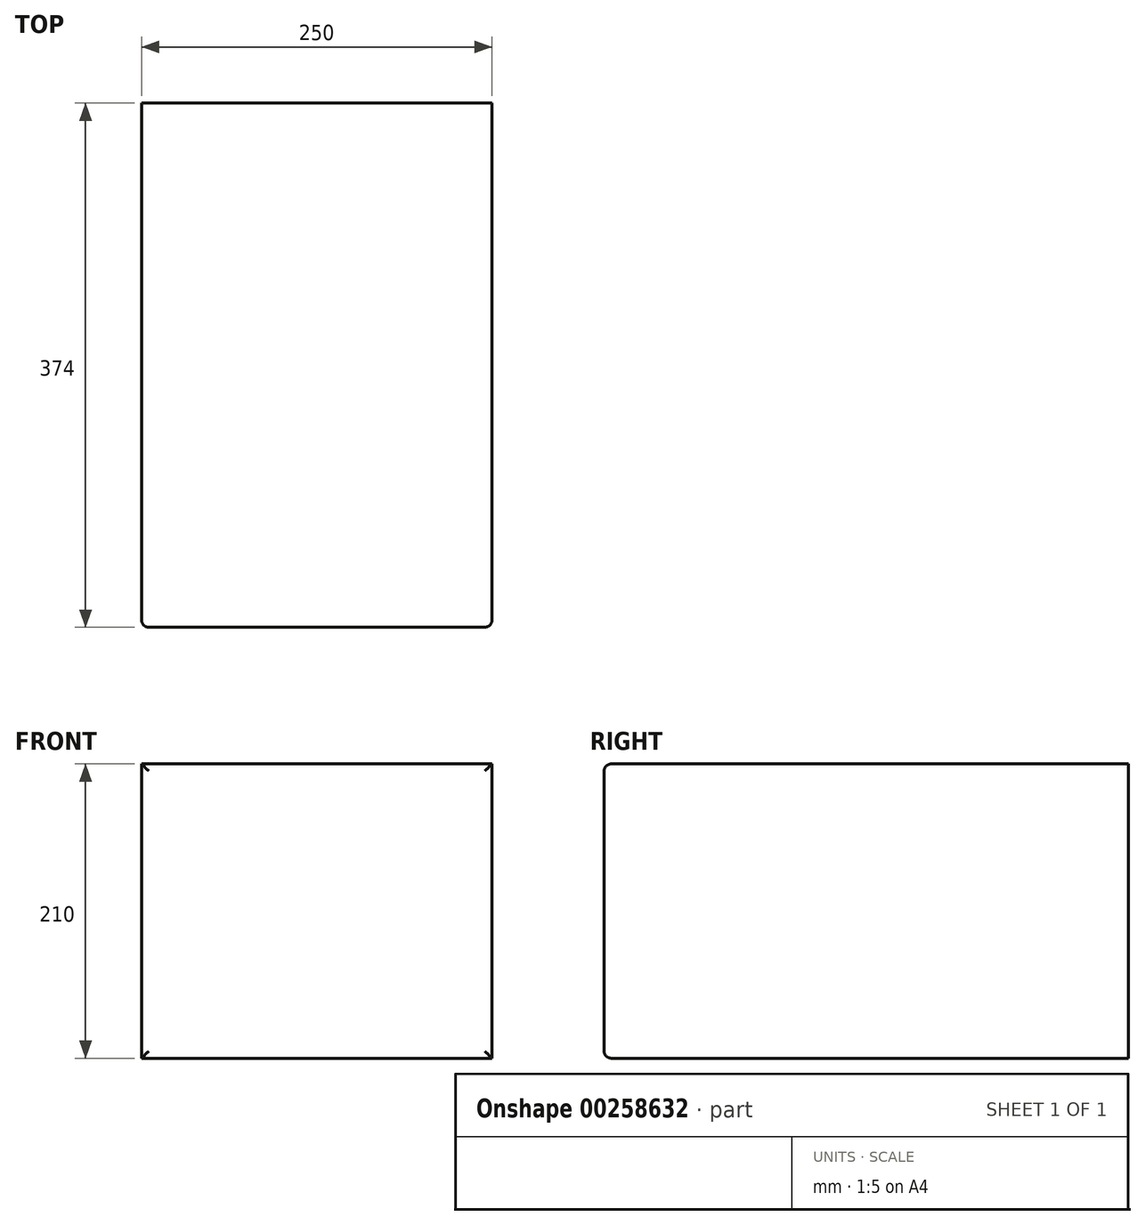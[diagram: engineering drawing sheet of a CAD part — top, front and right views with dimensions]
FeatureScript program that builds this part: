
annotation { "Feature Type Name" : "Feature", "Feature Type Description" : "" }
export const myFeature = defineFeature(function(context is Context, id is Id, definition is map)
    precondition{}
    {
        {
            var Q0;
            Q0=qCreatedBy(makeId("Top.planeOp"),FACE);
            var sketch = newSketch(context, id + "F0", { "sketchPlane" : qUnion([Q0])});
            skLineSegment(sketch, "E0.bottom", {"start": v(0, 0) * mm, "end": v(250, 0) * mm});
            skLineSegment(sketch, "E0.top", {"start": v(0, 374) * mm, "end": v(250, 374) * mm});
            skLineSegment(sketch, "E0.left", {"start": v(0, 0) * mm, "end": v(0, 374) * mm});
            skLineSegment(sketch, "E0.right", {"start": v(250, 0) * mm, "end": v(250, 374) * mm});
            skSolve(sketch);
        }
        {
            var Q0;
            Q0 = qSketchRegion(id + "F0", true);
            extrude(context, id + "F1", {"entities" : qUnion([Q0]), "depth" : 210 * mm});
        }
        {
            var Q0;
            Q0=makeQuery(id+"F1.opExtrude","SWEPT_FACE",FACE,{"disambiguationData":[OSD([sQuery(id+"F0.wireOp",EDGE,"E0.bottom")])]});
            fillet(context, id + "F2", {"entities" : qUnion([Q0]), "radius" : 5.08 * mm, "tangentPropagation" : true, "allowEdgeOverflow" : false});
        }
    });
